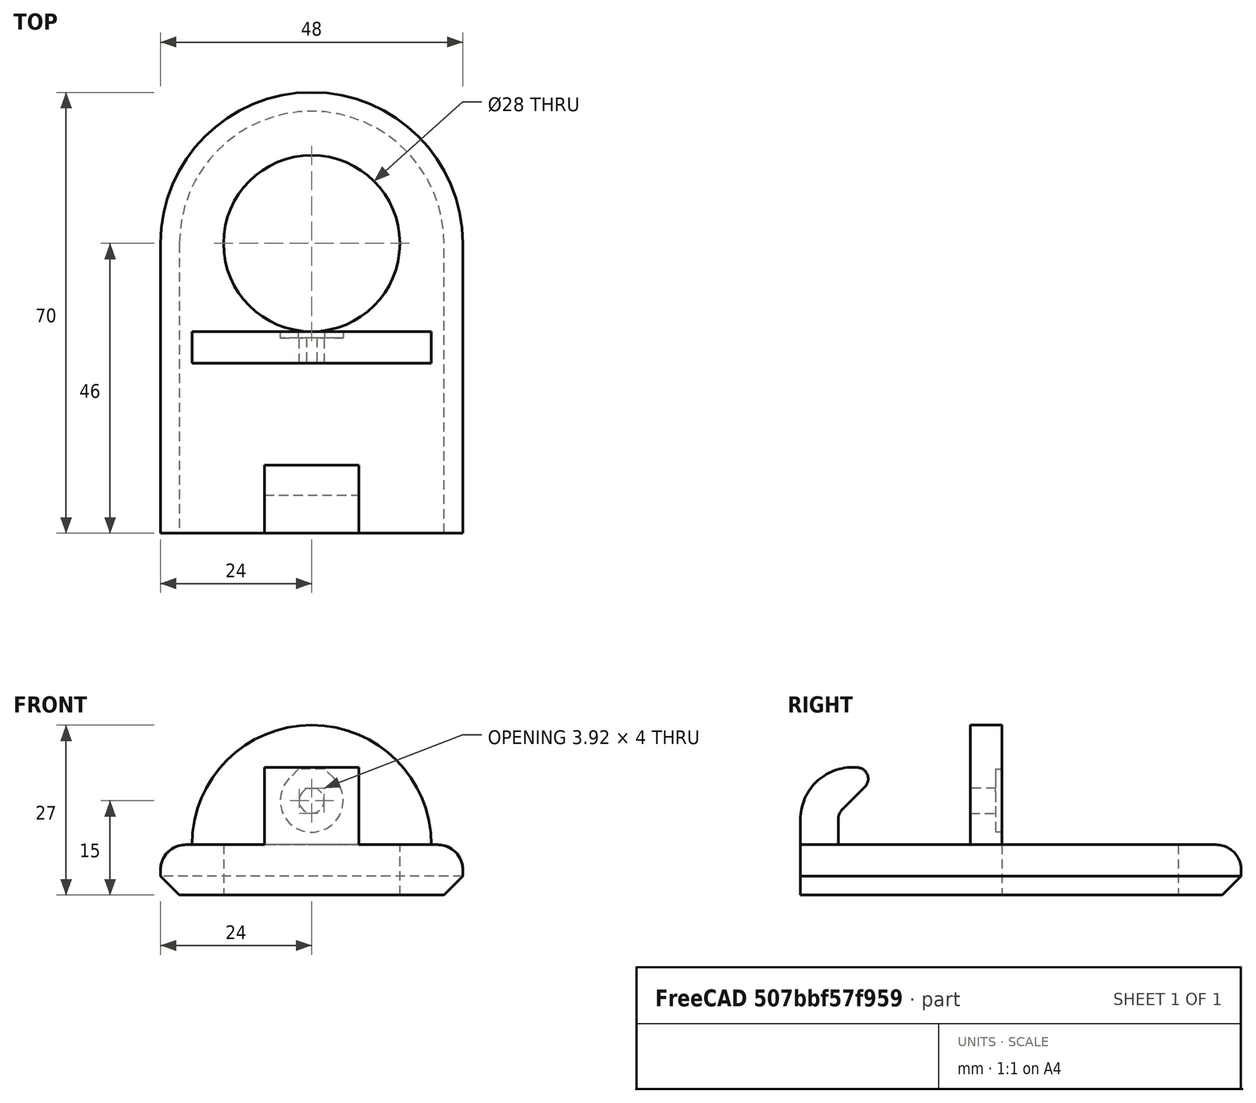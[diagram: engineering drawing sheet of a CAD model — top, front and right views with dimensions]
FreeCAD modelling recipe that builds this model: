
FCSTD DOCUMENT  (FreeCAD 0.16RUnknown)
Label: Hook
License: All rights reserved
LicenseURL: http://en.wikipedia.org/wiki/All_rights_reserved
objects: Sketcher::SketchObject×5, PartDesign::Pad×5, App::DocumentObjectGroup×3, Part::MultiFuse×3, Part::FeaturePython×3, Spreadsheet::Sheet×1, Mesh::Feature×1, Part::Fillet×1, Part::Chamfer×1, Part::Cut×1
note: 24 computed .brp shape members not serialized (recipe doc carries the construction recipe); baked Part::Feature solids carry a one-line shape summary decoded from their .brp

FEATURE [Spreadsheet::Sheet] Spreadsheet  label="pars"
  cells = A1=Bolts and Nuts; B1=Value; D1=Components; E1=Value; A2=Thread Tight Tolerance (Radius, ratio); B2(ThrTighRatio)=0.96; D2=Tight Cilinder Tolerances (Radius, mm); E2(CilTight)=0.1; A3=Thread Tight Tolerance (Radius, mm); B3(ThrTightmm)=0.1; D3=Loose Cilinder Tolerances (Radius, mm); E3(CilLoose)=0.1; A5=Nut Slot Width Clearance (mm); B5(NutWidthClearmm)=0.1; A6=Nut Slot Thickess Clearance (mm); B6(NutThickClearmm)=0.1; A13=Particular parameters; B13=Value
FEATURE [Mesh::Feature] Fase2_anilla
  Placement = pos=(715,502,-173.8) rot=(0,0,1;0rad)
FEATURE [App::DocumentObjectGroup] Group  label="Reference"
  Group = -> [Fase2_anilla]
FEATURE [Sketcher::SketchObject] Sketch  label="Main"
  sketch-geometry (5):
    g0: LineSegment StartX=-24 StartY=-6.74332e-07 StartZ=0 EndX=-24 EndY=-46 EndZ=0
    g1: LineSegment StartX=-24 StartY=-46 StartZ=0 EndX=24 EndY=-46 EndZ=0
    g2: LineSegment StartX=24 StartY=-46 StartZ=0 EndX=24 EndY=-7.29941e-07 EndZ=0
    g3: ArcOfCircle CenterX=0 CenterY=0 CenterZ=0 NormalX=0 NormalY=0 NormalZ=1 Radius=24 StartAngle=6.28319 EndAngle=9.42478
    g4: Circle CenterX=0 CenterY=0 CenterZ=0 NormalX=0 NormalY=0 NormalZ=1 Radius=14
  constraints (14):
    c: Coincident(g0,g1)
    c: Coincident(g1,g2)
    c: Coincident(g3,g4)
    c: Coincident(g3,g-1)
    c: Coincident(g2,g3)
    c: Coincident(g0,g3)
    c: Tangent(g2,g3)
    c: Tangent(g0,g3)
    c: Horizontal(g1)
    c: Vertical(g2)
    c: Vertical(g0)
    c: Radius(g4) = 14
    c: Radius(g3) = 24
    c: DistanceY(g1) = -46
FEATURE [PartDesign::Pad] Pad  label="Main001"
  Length = 8
  Length2 = 100
  Sketch = -> Sketch
  Type = 0
FEATURE [Part::Fillet] Fillet  label="MainFillet"
  Base = -> Pad
  Edges = 1 edges r=4: [Edge10]
FEATURE [Part::Chamfer] Chamfer  label="MainChamfer"
  Base = -> Fillet
  Edges = 1 edges r=3: [Edge12]
FEATURE [Sketcher::SketchObject] Sketch001  label="BoltPad"
  Placement = pos=(0,-14,8) rot=(1,0,0;1.5708rad)
  sketch-geometry (2):
    g0: ArcOfCircle CenterX=0 CenterY=0 CenterZ=0 NormalX=0 NormalY=0 NormalZ=1 Radius=19 StartAngle=0 EndAngle=3.14159
    g1: LineSegment StartX=-19 StartY=0 StartZ=0 EndX=19 EndY=0 EndZ=0
  constraints (6):
    c: Coincident(g0,g1)
    c: Coincident(g0,g1)
    c: Horizontal(g1)
    c: PointOnObject(g0,g1)
    c: Coincident(g0,g-1)
    c: Radius(g0) = 19
FEATURE [PartDesign::Pad] Pad001  label="BoltPad001"
  Length = 5
  Length2 = 100
  Placement = pos=(0,-14,8) rot=(1,0,0;1.5708rad)
  Sketch = -> Sketch001
  Type = 0
FEATURE [Part::MultiFuse] Fusion  label="BoltPadFusion"
  Shapes = -> [Pad001,Chamfer]
FEATURE [Sketcher::SketchObject] Sketch002  label="PrintBoltHole"
  sketch-geometry (4):
    g0: ArcOfCircle CenterX=0 CenterY=0 CenterZ=0 NormalX=0 NormalY=0 NormalZ=1 Radius=2 StartAngle=2.35619 EndAngle=7.06859
    g1: LineSegment StartX=-1.41421 StartY=1.41422 StartZ=0 EndX=-0.828427 EndY=2 EndZ=0
    g2: LineSegment StartX=-0.828427 StartY=2 StartZ=0 EndX=0.828427 EndY=2 EndZ=0
    g3: LineSegment StartX=0.828427 StartY=2 StartZ=0 EndX=1.41421 EndY=1.41422 EndZ=0
  constraints (12):
    c: Coincident(g1,g2)
    c: Coincident(g2,g3)
    c: Coincident(g0,g1)
    c: Coincident(g0,g3)
    c: Tangent(g0,g1)
    c: Coincident(g0,g-1)
    c: Tangent(g3,g0)
    c: Horizontal(g2)
    c: Tangent(g2,g0)
    c: Perpendicular(g1,g3)
    c: Angle(g1,g2) = 2.35619
    c: Radius(g0) = 2
FEATURE [PartDesign::Pad] Pad002  label="PrintBoltHole001"
  Length = 20
  Length2 = 100
  Reversed = true
  Sketch = -> Sketch002
  Type = 0
FEATURE [Sketcher::SketchObject] Sketch003  label="PrintBoltHead"
  sketch-geometry (4):
    g0: ArcOfCircle CenterX=0 CenterY=0 CenterZ=0 NormalX=0 NormalY=0 NormalZ=1 Radius=5 StartAngle=2.35619 EndAngle=7.06858
    g1: LineSegment StartX=-3.53553 StartY=3.53554 StartZ=0 EndX=-2.07107 EndY=5 EndZ=0
    g2: LineSegment StartX=-2.07107 StartY=5 StartZ=0 EndX=2.07107 EndY=5 EndZ=0
    g3: LineSegment StartX=2.07107 StartY=5 StartZ=0 EndX=3.53555 EndY=3.53552 EndZ=0
  constraints (12):
    c: Coincident(g1,g2)
    c: Coincident(g2,g3)
    c: Coincident(g0,g1)
    c: Coincident(g0,g3)
    c: Tangent(g0,g1)
    c: Coincident(g0,g-1)
    c: Tangent(g3,g0)
    c: Horizontal(g2)
    c: Tangent(g2,g0)
    c: Perpendicular(g1,g3)
    c: Angle(g1,g2) = 2.35619
    c: Radius(g0) = 5
FEATURE [PartDesign::Pad] Pad003  label="PrintBoltHead001"
  Length = 10
  Length2 = 100
  Sketch = -> Sketch003
  Type = 0
FEATURE [Part::MultiFuse] Fusion001  label="PrintBoltSlot"
  Shapes = -> [Pad002,Pad003]
FEATURE [App::DocumentObjectGroup] Group002  label="Component_src"
  Group = -> [Fusion001]
FEATURE [Part::FeaturePython] Clone  label="Clone of PrintBoltSlot"  # Draft clone (typed FeaturePython)
  Objects = -> [Fusion001]
  Placement = pos=(0,-15,15) rot=(0,0.707107,0.707107;3.14159rad)
  Scale = (1,1,1)
FEATURE [Part::Cut] Cut  label="BoltSlotCut"
  Base = -> Fusion
  Tool = -> Clone
FEATURE [Sketcher::SketchObject] Sketch004  label="HookPad"
  Placement = pos=(0,0,0) rot=(0.57735,0.57735,0.57735;2.0944rad)
  sketch-geometry (7):
    g0: LineSegment StartX=-40 StartY=0 StartZ=0 EndX=-40 EndY=12 EndZ=0
    g1: LineSegment StartX=-40 StartY=0 StartZ=0 EndX=-46 EndY=0 EndZ=0
    g2: LineSegment StartX=-46 StartY=0 StartZ=0 EndX=-46 EndY=12 EndZ=0
    g3: ArcOfCircle CenterX=-37.7 CenterY=12 CenterZ=0 NormalX=0 NormalY=0 NormalZ=1 Radius=2.3 StartAngle=2.35619 EndAngle=3.14159
    g4: ArcOfCircle CenterX=-37.7 CenterY=12 CenterZ=0 NormalX=0 NormalY=0 NormalZ=1 Radius=8.3 StartAngle=1.46794 EndAngle=3.14159
    g5: ArcOfCircle CenterX=-37.0326 CenterY=18.4656 CenterZ=0 NormalX=0 NormalY=0 NormalZ=1 Radius=1.8 StartAngle=5.49778 EndAngle=7.75112
    g6: LineSegment StartX=-39.3263 StartY=13.6264 StartZ=0 EndX=-35.7598 EndY=17.1928 EndZ=0
  constraints (23):
    c: Coincident(g1,g2)
    c: Coincident(g1,g0)
    c: PointOnObject(g1,g-1)
    c: Horizontal(g1)
    c: Vertical(g0)
    c: Vertical(g2)
    c: DistanceX(g1) = -46
    c: DistanceX(g1,g1) = 6
    c: Coincident(g0,g3)
    c: Coincident(g2,g4)
    c: Tangent(g4,g2)
    c: Tangent(g0,g3)
    c: Coincident(g3,g4)
    c: Coincident(g4,g5)
    c: Angle(g6) = 0.785398
    c: Coincident(g3,g6)
    c: Coincident(g5,g6)
    c: Tangent(g3,g6)
    c: Tangent(g5,g6)
    c: Tangent(g4,g5)
    c: DistanceY(g2,g2) = 12
    c: Radius(g5) = 1.8
    c: Radius(g3) = 2.3
FEATURE [PartDesign::Pad] Pad004  label="HookPad001"
  Length = 15
  Length2 = 100
  Midplane = true
  Placement = pos=(0,0,0) rot=(0.57735,0.57735,0.57735;2.0944rad)
  Sketch = -> Sketch004
  Type = 0
FEATURE [Part::MultiFuse] Fusion002  label="HookAdd"
  Shapes = -> [Cut,Pad004]
FEATURE [Part::FeaturePython] refine  label="refine_HookAdd"  # WARN: FeaturePython — macro-defined, semantics opaque (R4)
  Base = -> Fusion002
FEATURE [App::DocumentObjectGroup] Group001  label="src"
  Group = -> [Pad,Fusion002,refine]
FEATURE [Part::FeaturePython] Clone001  label="Hook"  # Draft clone (typed FeaturePython)
  Objects = -> [refine]
  Scale = (1,1,1)
